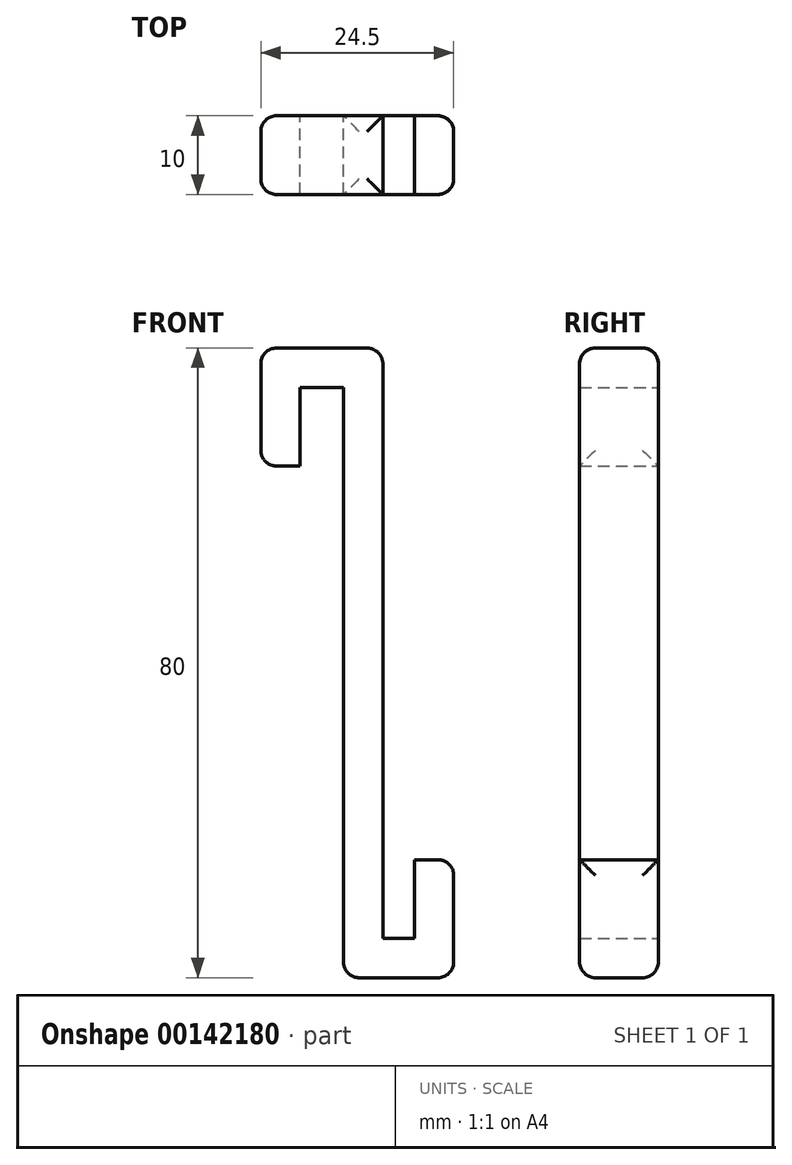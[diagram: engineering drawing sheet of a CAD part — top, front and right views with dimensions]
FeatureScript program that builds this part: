
annotation { "Feature Type Name" : "Feature", "Feature Type Description" : "" }
export const myFeature = defineFeature(function(context is Context, id is Id, definition is map)
    precondition{}
    {
        {
            var Q0;
            Q0=qCreatedBy(makeId("Front.planeOp"),FACE);
            var sketch = newSketch(context, id + "F0", { "sketchPlane" : qUnion([Q0])});
            skLineSegment(sketch, "E0", {"start": v(0, 0) * mm, "end": v(0, 15) * mm});
            skLineSegment(sketch, "E1", {"start": v(0, 15) * mm, "end": v(15.5, 15) * mm});
            skLineSegment(sketch, "E2", {"start": v(0, 0) * mm, "end": v(5, 0) * mm});
            skLineSegment(sketch, "E3", {"start": v(5, 0) * mm, "end": v(5, 10) * mm});
            skLineSegment(sketch, "E4", {"start": v(5, 10) * mm, "end": v(10.5, 10) * mm});
            skLineSegment(sketch, "E5", {"start": v(10.5, 10) * mm, "end": v(10.5, -65) * mm});
            skLineSegment(sketch, "E6", {"start": v(10.5, -65) * mm, "end": v(24.5, -65) * mm});
            skLineSegment(sketch, "E7", {"start": v(24.5, -65) * mm, "end": v(24.5, -50) * mm});
            skLineSegment(sketch, "E8", {"start": v(24.5, -50) * mm, "end": v(19.5, -50) * mm});
            skLineSegment(sketch, "E9", {"start": v(19.5, -50) * mm, "end": v(19.5, -60) * mm});
            skLineSegment(sketch, "E10", {"start": v(19.5, -60) * mm, "end": v(15.5, -60) * mm});
            skLineSegment(sketch, "E11", {"start": v(15.5, -60) * mm, "end": v(15.5, 15) * mm});
            skSolve(sketch);
        }
        {
            var Q0;
            Q0 = qSketchRegion(id + "F0", true);
            extrude(context, id + "F1", {"entities" : qUnion([Q0]), "depth" : 10 * mm});
        }
        {
            var Q0;
            Q0=makeQuery(id+"F1.opExtrude","SWEPT_EDGE",EDGE,{"disambiguationData":[OSD([sQuery(id+"F0.wireOp",EDGE,"E0"),sQuery(id+"F0.wireOp",EDGE,"E1")])]});
            var Q1;
            Q1=makeQuery(id+"F1.opExtrude","SWEPT_EDGE",EDGE,{"disambiguationData":[OSD([sQuery(id+"F0.wireOp",EDGE,"E1"),sQuery(id+"F0.wireOp",EDGE,"E11")])]});
            var Q2;
            Q2=makeQuery(id+"F1.opExtrude","SWEPT_EDGE",EDGE,{"disambiguationData":[OSD([sQuery(id+"F0.wireOp",EDGE,"E5"),sQuery(id+"F0.wireOp",EDGE,"E6")])]});
            var Q3;
            Q3=makeQuery(id+"F1.opExtrude","SWEPT_EDGE",EDGE,{"disambiguationData":[OSD([sQuery(id+"F0.wireOp",EDGE,"E7"),sQuery(id+"F0.wireOp",EDGE,"E8")])]});
            var Q4;
            Q4=makeQuery(id+"F1.opExtrude","SWEPT_EDGE",EDGE,{"disambiguationData":[OSD([sQuery(id+"F0.wireOp",EDGE,"E6"),sQuery(id+"F0.wireOp",EDGE,"E7")])]});
            var Q5;
            Q5=makeQuery(id+"F1.opExtrude","SWEPT_EDGE",EDGE,{"disambiguationData":[OSD([sQuery(id+"F0.wireOp",EDGE,"E0"),sQuery(id+"F0.wireOp",EDGE,"E2")])]});
            var Q6;
            Q6=makeQuery(id+"F1.opExtrude","CAP_EDGE",EDGE,{"disambiguationData":[OSD([sQuery(id+"F0.wireOp",EDGE,"E0")])],"isStart":false});
            var Q7;
            Q7=makeQuery(id+"F1.opExtrude","CAP_EDGE",EDGE,{"disambiguationData":[OSD([sQuery(id+"F0.wireOp",EDGE,"E0")])],"isStart":true});
            var Q8;
            Q8=makeQuery(id+"F1.opExtrude","CAP_EDGE",EDGE,{"disambiguationData":[OSD([sQuery(id+"F0.wireOp",EDGE,"E7")])],"isStart":true});
            var Q9;
            Q9=makeQuery(id+"F1.opExtrude","CAP_EDGE",EDGE,{"disambiguationData":[OSD([sQuery(id+"F0.wireOp",EDGE,"E7")])],"isStart":false});
            var Q10;
            Q10=makeQuery(id+"F1.opExtrude","CAP_EDGE",EDGE,{"disambiguationData":[OSD([sQuery(id+"F0.wireOp",EDGE,"E6")])],"isStart":false});
            var Q11;
            Q11=makeQuery(id+"F1.opExtrude","CAP_EDGE",EDGE,{"disambiguationData":[OSD([sQuery(id+"F0.wireOp",EDGE,"E6")])],"isStart":true});
            var Q12;
            Q12=makeQuery(id+"F1.opExtrude","CAP_EDGE",EDGE,{"disambiguationData":[OSD([sQuery(id+"F0.wireOp",EDGE,"E1")])],"isStart":false});
            var Q13;
            Q13=makeQuery(id+"F1.opExtrude","CAP_EDGE",EDGE,{"disambiguationData":[OSD([sQuery(id+"F0.wireOp",EDGE,"E1")])],"isStart":true});
            fillet(context, id + "F2", {"entities" : qUnion([Q0, Q1, Q2, Q3, Q4, Q5, Q6, Q7, Q8, Q9, Q10, Q11, Q12, Q13]), "radius" : 2 * mm, "tangentPropagation" : true, "allowEdgeOverflow" : false});
        }
    });
